# Revit family: Urinal-PhotocellUrinal-Vitra-ArkitektSeries-5999
name_source: partatom
category: Plumbing Fixtures
revit_build: Autodesk Revit 2017 (Build: 20160225_1515(x64)
units: mm (PartAtom-declared; Revit-internal decimal feet)

## family parameters
Cut with Voids When Loaded = No
Host = Face
OmniClass Number = 23.45.05.14.14
OmniClass Title = Sinks/Lavatories
Part Type = Normal
Room Calculation Point = No
Round Connector Dimension = Use Diameter
Shared = Yes

## types (10) — shared parameters
BIMobject category = Urinals
Brand = VitrA
CW Connection = No
Color = White
Default Elevation = 650 mm
Description = VitrA Arkitekt Urinal with Integrated Infrared Flush Sensor
Design country = Turkey
HW Connection = No
IFC Classification = Sanitary Terminal
Main Material = Ceramic
Manufacturer = Vitra
Manufacturer name = Vitra
Masterformat 2014 Code = 22 41 13.16
Masterformat 2014 Description = Residential Urinals
Mounting type = Wall Mounted Urinal
NBS Referans Code = 31-93
NBS Referans Description = Urinal And Wc Fittings
Nominal Depth (mm) = 360 mm
Nominal Height (mm) = 680 mm  [stored 2.23097 ft]
Nominal Width (mm) = 405 mm
OmniClass Code = 23-31 21 00
OmniClass Description = Urinals
Primary Material = <By Category>
Product certification = https://www.vitraglobal.com
Product family = Wall Mounted Urinal
Product group = Arkitekt
Secondary Material = White
URL = https://www.vitra.com.tr
Uniclass 1.4 Code = L721
Uniclass 1.4 Description = Sanitary equipment
Uniclass 2.0 Code = PR-31-93
Uniclass 2.0 Description = Urinal And Wc Fittings
Uniclass 2015 Code = Pr_40_20_93
Uniclass 2015 Name = Urinal and WC fittings
Uniformat II Code = D2010
Uniformat II Description = Plumbing Fixtures
Vent Connection = No
Warranty Period (Year) = 10 Years
Waste Connection = No
Weight Net (kg) = 27.93
Youtube = https://www.youtube.com

## per-type parameters (varying)
| type | Article No. (default) | Model | Product SKU | Product url | Technical description |
| Urinal_Vitra_Arkitekt_5999B003H5558 | 5999B003H5558 | 5999B003H5558 | 5999B003H5558 | https://www.vitra-india.com | https://www.vitra-india.com |
| Urinal_Vitra_Arkitekt_5999B003H5557 | 5999B003H5557 | 5999B003H5557 | 5999B003H5557 | https://www.vitra-india.com | https://www.vitra-india.com |
| Urinal_Vitra_Arkitekt_5999B003H5556 | 5999B003H5556 | 5999B003H5556 | 5999B003H5556 | https://www.vitra-india.com | https://www.vitra-india.com |
| Urinal_Vitra_Arkitekt_5999B003H5555 | 5999B003H5555 | 5999B003H5555 | 5999B003H5555 | https://www.vitra-india.com | https://www.vitra-india.com |
| Urinal_Vitra_Arkitekt_5999B403-5556 | 5999B403-5556 | 5999B403-5556 | 5999B403-5556 | https://www.vitraglobal.com | https://www.vitraglobal.com |
| Urinal_Vitra_Arkitekt_5999B003-5558 | 5999B003-5558 | 5999B003-5558 | 5999B003-5558 | https://www.vitraglobal.com | https://www.vitraglobal.com |
| Urinal_Vitra_Arkitekt_5999B003-5556 | 5999B003-5556 | 5999B003-5556 | 5999B003-5556 | https://www.vitraglobal.com | https://www.vitraglobal.com |
| Urinal_Vitra_Arkitekt_5999B403-5555 | 5999B403-5555 | 5999B403-5555 | 5999B403-5555 | https://www.vitraglobal.com | https://www.vitraglobal.com |
| Urinal_Vitra_Arkitekt_5999B003-5557 | 5999B003-5557 | 5999B003-5557 | 5999B003-5557 | https://www.vitraglobal.com | https://www.vitraglobal.com |
| Urinal_Vitra_Arkitekt_5999B003-5555 | 5999B003-5555 | 5999B003-5555 | 5999B003-5555 | https://www.vitraglobal.com | https://www.vitraglobal.com |

note: [stored X ft] marks values corroborated as IEEE doubles in the binary element streams (Revit-internal decimal feet)

## geometry (parser evidence)
native form markers: Sweep x3
no freeform markers — native parametric forms only
